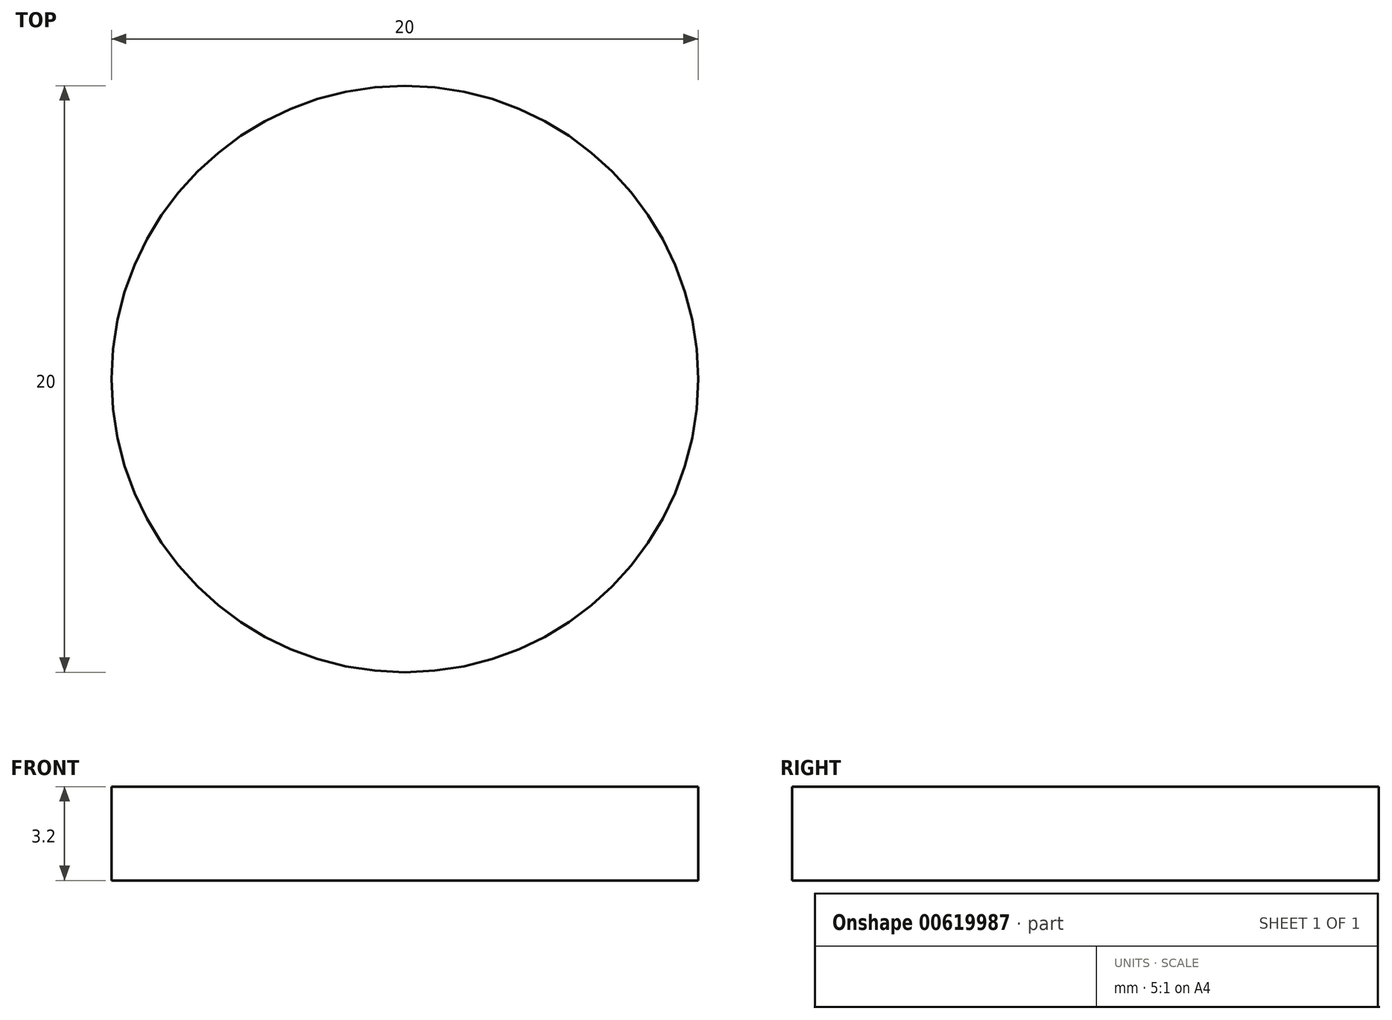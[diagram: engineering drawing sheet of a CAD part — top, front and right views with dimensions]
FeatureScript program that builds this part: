
annotation { "Feature Type Name" : "Feature", "Feature Type Description" : "" }
export const myFeature = defineFeature(function(context is Context, id is Id, definition is map)
    precondition{}
    {
        {
            var Q0;
            Q0=qCreatedBy(makeId("Top.planeOp"),FACE);
            var sketch = newSketch(context, id + "F0", { "sketchPlane" : qUnion([Q0])});
            skCircle(sketch, "E0", {"center": v(0, 0) * mm, "radius": 10 * mm});
            skSolve(sketch);
        }
        {
            var Q0;
            Q0 = qSketchRegion(id + "F0", true);
            extrude(context, id + "F1", {"entities" : qUnion([Q0]), "depth" : 3.2 * mm, "offsetDistance" : 25 * mm});
        }
    });
